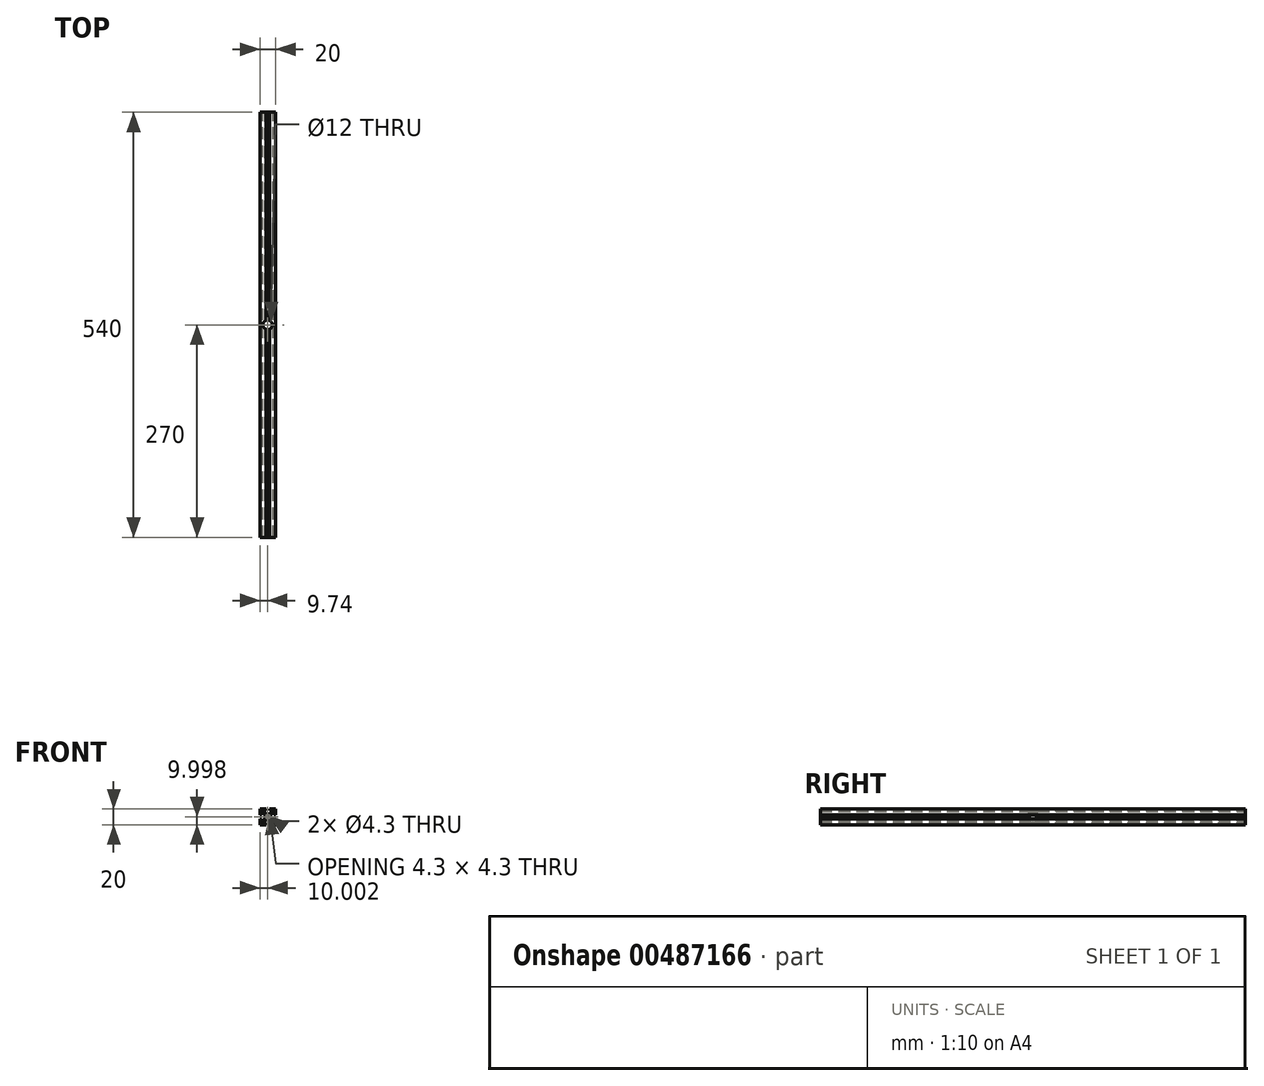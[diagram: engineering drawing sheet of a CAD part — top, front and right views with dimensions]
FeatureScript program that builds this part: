
annotation { "Feature Type Name" : "Feature", "Feature Type Description" : "" }
export const myFeature = defineFeature(function(context is Context, id is Id, definition is map)
    precondition{}
    {
        {
            var Q0;
            Q0=qCreatedBy(makeId("Front.planeOp"),FACE);
            var sketch = newSketch(context, id + "F0", { "sketchPlane" : qUnion([Q0])});
            skLineSegment(sketch, "E0.bottom", {"start": v(-9.74, 9.77) * mm, "end": v(-2.24, 9.77) * mm});
            skLineSegment(sketch, "E0.left", {"start": v(-9.74, 9.77) * mm, "end": v(-9.74, 2.27) * mm});
            skLineSegment(sketch, "E0.right", {"start": v(10.26, 9.77) * mm, "end": v(10.26, 2.27) * mm});
            skArc(sketch, "E1", {"start": v(2.41, -0.23) * mm, "mid": v(0.26, 1.92) * mm, "end": v(-1.89, -0.23) * mm});
            skLineSegment(sketch, "E2.bottom", {"start": v(-1.97, 3.42) * mm, "end": v(2.5, 3.42) * mm});
            skLineSegment(sketch, "E2.left", {"start": v(-3.39, 2) * mm, "end": v(-3.39, -0.23) * mm});
            skLineSegment(sketch, "E2.right", {"start": v(3.91, 2) * mm, "end": v(3.91, -0.23) * mm});
            skLineSegment(sketch, "E3", {"start": v(-2.24, 9.77) * mm, "end": v(-2.24, 7.77) * mm});
            skLineSegment(sketch, "E4", {"start": v(-2.24, 7.77) * mm, "end": v(-6.32, 7.77) * mm});
            skLineSegment(sketch, "E5", {"start": v(2.76, 9.77) * mm, "end": v(2.76, 7.77) * mm});
            skPoint(sketch, "E5.endSnap0", {"position": v(-5.99, 7.77) * mm});
            skLineSegment(sketch, "E6", {"start": v(2.76, 7.77) * mm, "end": v(6.85, 7.77) * mm});
            skLineSegment(sketch, "E7", {"start": v(-7.74, 6.35) * mm, "end": v(-7.74, 2.27) * mm});
            skLineSegment(sketch, "E8", {"start": v(-7.74, 2.27) * mm, "end": v(-9.74, 2.27) * mm});
            skLineSegment(sketch, "E9", {"start": v(-7.74, 6.35) * mm, "end": v(-3.39, 2) * mm});
            skLineSegment(sketch, "E10", {"start": v(-1.97, 3.42) * mm, "end": v(-6.32, 7.77) * mm});
            skPoint(sketch, "E10.endSnap0", {"position": v(-6.32, -0.18) * mm});
            skLineSegment(sketch, "E11", {"start": v(8.26, 6.35) * mm, "end": v(8.26, 2.27) * mm});
            skLineSegment(sketch, "E12", {"start": v(8.26, 2.27) * mm, "end": v(10.26, 2.27) * mm});
            skPoint(sketch, "E13.orphan", {"position": v(10.26, 7.77) * mm});
            skLineSegment(sketch, "E14", {"start": v(2.5, 3.42) * mm, "end": v(6.85, 7.77) * mm});
            skLineSegment(sketch, "E15", {"start": v(3.91, 2) * mm, "end": v(8.26, 6.35) * mm});
            skPoint(sketch, "E16.orphan", {"position": v(-9.74, 7.77) * mm});
            skPoint(sketch, "E17.orphan", {"position": v(-3.39, 3.42) * mm});
            skPoint(sketch, "E18.orphan", {"position": v(3.91, 3.42) * mm});
            skLineSegment(sketch, "E19", {"start": v(-9.74, -0.23) * mm, "end": v(10.26, -0.23) * mm, "construction": true});
            skPoint(sketch, "E0.top.end.orphan", {"position": v(10.26, -10.23) * mm});
            skPoint(sketch, "E0.top.start.orphan", {"position": v(-9.74, -10.23) * mm});
            skLineSegment(sketch, "E20.MirrorCS", {"start": v(-9.74, -10.23) * mm, "end": v(-9.74, -2.73) * mm});
            skLineSegment(sketch, "E21.MirrorCS", {"start": v(-7.74, -2.73) * mm, "end": v(-9.74, -2.73) * mm});
            skLineSegment(sketch, "E22.MirrorCS", {"start": v(-7.74, -6.82) * mm, "end": v(-7.74, -2.73) * mm});
            skLineSegment(sketch, "E23.MirrorCS", {"start": v(-7.74, -6.82) * mm, "end": v(-3.39, -2.47) * mm});
            skLineSegment(sketch, "E24.MirrorCS", {"start": v(-3.39, -2.47) * mm, "end": v(-3.39, -0.23) * mm});
            skArc(sketch, "E25.MirrorCS", {"start": v(2.41, -0.23) * mm, "mid": v(0.26, -2.38) * mm, "end": v(-1.89, -0.23) * mm});
            skLineSegment(sketch, "E26.MirrorCS", {"start": v(-1.97, -3.88) * mm, "end": v(-6.32, -8.23) * mm});
            skLineSegment(sketch, "E27.MirrorCS", {"start": v(-1.97, -3.88) * mm, "end": v(2.5, -3.88) * mm});
            skLineSegment(sketch, "E28.MirrorCS", {"start": v(-2.24, -8.23) * mm, "end": v(-6.32, -8.23) * mm});
            skLineSegment(sketch, "E29.MirrorCS", {"start": v(-2.24, -10.23) * mm, "end": v(-2.24, -8.23) * mm});
            skLineSegment(sketch, "E30.MirrorCS", {"start": v(-9.74, -10.23) * mm, "end": v(-2.24, -10.23) * mm});
            skLineSegment(sketch, "E31.MirrorCS", {"start": v(2.76, -10.23) * mm, "end": v(2.76, -8.23) * mm});
            skLineSegment(sketch, "E32.MirrorCS", {"start": v(2.76, -8.23) * mm, "end": v(6.85, -8.23) * mm});
            skLineSegment(sketch, "E33.MirrorCS", {"start": v(2.5, -3.88) * mm, "end": v(6.85, -8.23) * mm});
            skLineSegment(sketch, "E34.MirrorCS", {"start": v(3.91, -2.47) * mm, "end": v(8.26, -6.82) * mm});
            skLineSegment(sketch, "E35.MirrorCS", {"start": v(8.26, -6.82) * mm, "end": v(8.26, -2.73) * mm});
            skLineSegment(sketch, "E36.MirrorCS", {"start": v(8.26, -2.73) * mm, "end": v(10.26, -2.73) * mm});
            skLineSegment(sketch, "E37.MirrorCS", {"start": v(10.26, -10.23) * mm, "end": v(10.26, -2.73) * mm});
            skLineSegment(sketch, "E38.MirrorCS", {"start": v(3.91, -2.47) * mm, "end": v(3.91, -0.23) * mm});
            skLineSegment(sketch, "E39.trimOffspring", {"start": v(2.76, 9.77) * mm, "end": v(10.26, 9.77) * mm});
            skLineSegment(sketch, "E40.trimOffspring", {"start": v(2.76, -10.23) * mm, "end": v(10.26, -10.23) * mm});
            skSolve(sketch);
        }
        {
            var Q0;
            Q0=makeQuery(id+"F0.imprint","IMPRINT",FACE,{"disambiguationData":[TD([[makeQuery(id+"F0.imprint","IMPRINT",EDGE,{"derivedFrom":sQuery(id+"F0.wireOp",EDGE,"E0.bottom")}),-1.0]])]});
            extrude(context, id + "F1", {"entities" : qUnion([Q0]), "depth" : 270 * mm, "hasSecondDirection" : true, "secondDirectionOppositeDirection" : true, "secondDirectionDepth" : 270 * mm});
        }
        {
            var Q0;
            Q0=qCreatedBy(makeId("Top.planeOp"),FACE);
            var sketch = newSketch(context, id + "F2", { "sketchPlane" : qUnion([Q0])});
            skCircle(sketch, "E41", {"center": v(0, 0) * mm, "radius": 6 * mm});
            skSolve(sketch);
        }
        {
            var Q0;
            Q0 = qSketchRegion(id + "F2", true);
            extrude(context, id + "F3", {"entities" : qUnion([Q0]), "operationType" : NewBodyOperationType.REMOVE, "oppositeDirection" : true, "depth" : 25 * mm, "hasSecondDirection" : true, "secondDirectionOppositeDirection" : false, "secondDirectionDepth" : 25 * mm});
        }
    });
